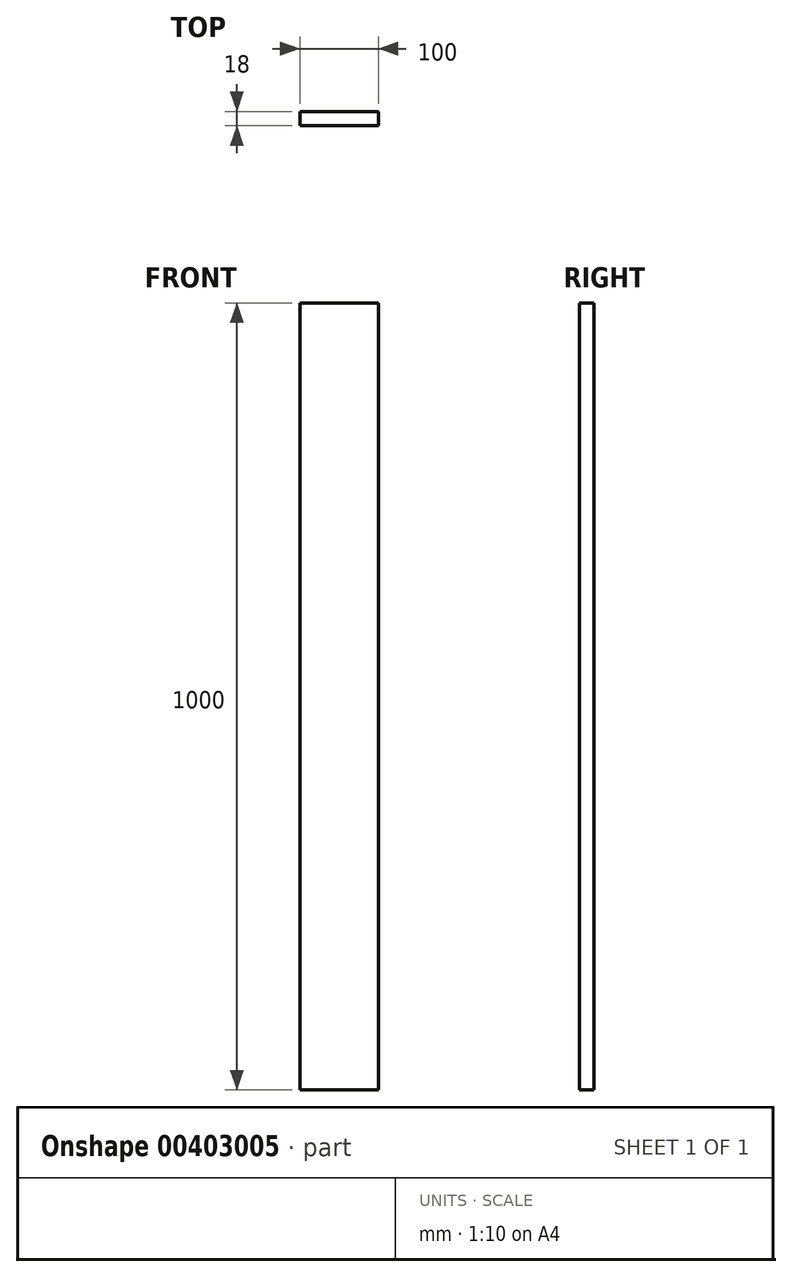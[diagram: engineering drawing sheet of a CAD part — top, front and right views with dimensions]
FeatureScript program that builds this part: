
annotation { "Feature Type Name" : "Feature", "Feature Type Description" : "" }
export const myFeature = defineFeature(function(context is Context, id is Id, definition is map)
    precondition{}
    {
        {
            var Q0;
            Q0=qCreatedBy(makeId("Front.planeOp"),FACE);
            var sketch = newSketch(context, id + "F0", { "sketchPlane" : qUnion([Q0])});
            skLineSegment(sketch, "E0.bottom", {"start": v(0, 0) * mm, "end": v(100, 0) * mm});
            skLineSegment(sketch, "E0.top", {"start": v(0, 1000) * mm, "end": v(100, 1000) * mm});
            skLineSegment(sketch, "E0.left", {"start": v(0, 0) * mm, "end": v(0, 1000) * mm});
            skLineSegment(sketch, "E0.right", {"start": v(100, 0) * mm, "end": v(100, 1000) * mm});
            skSolve(sketch);
        }
        {
            var Q0;
            Q0=makeQuery(id+"F0.imprint","IMPRINT",FACE,{"disambiguationData":[TD([[makeQuery(id+"F0.imprint","IMPRINT",EDGE,{"derivedFrom":sQuery(id+"F0.wireOp",EDGE,"kHmZVxOG-gPJc-REYJ-O9rl-HYASeAGw87Q2.bottom")}),1.0]])]});
            var Q1;
            Q1=makeQuery(id+"F0.imprint","IMPRINT",FACE,{"disambiguationData":[TD([[makeQuery(id+"F0.imprint","IMPRINT",EDGE,{"derivedFrom":sQuery(id+"F0.wireOp",EDGE,"E0.bottom")}),1.0]])]});
            extrude(context, id + "F1", {"entities" : qUnion([Q0, Q1]), "depth" : 18 * mm});
        }
    });
